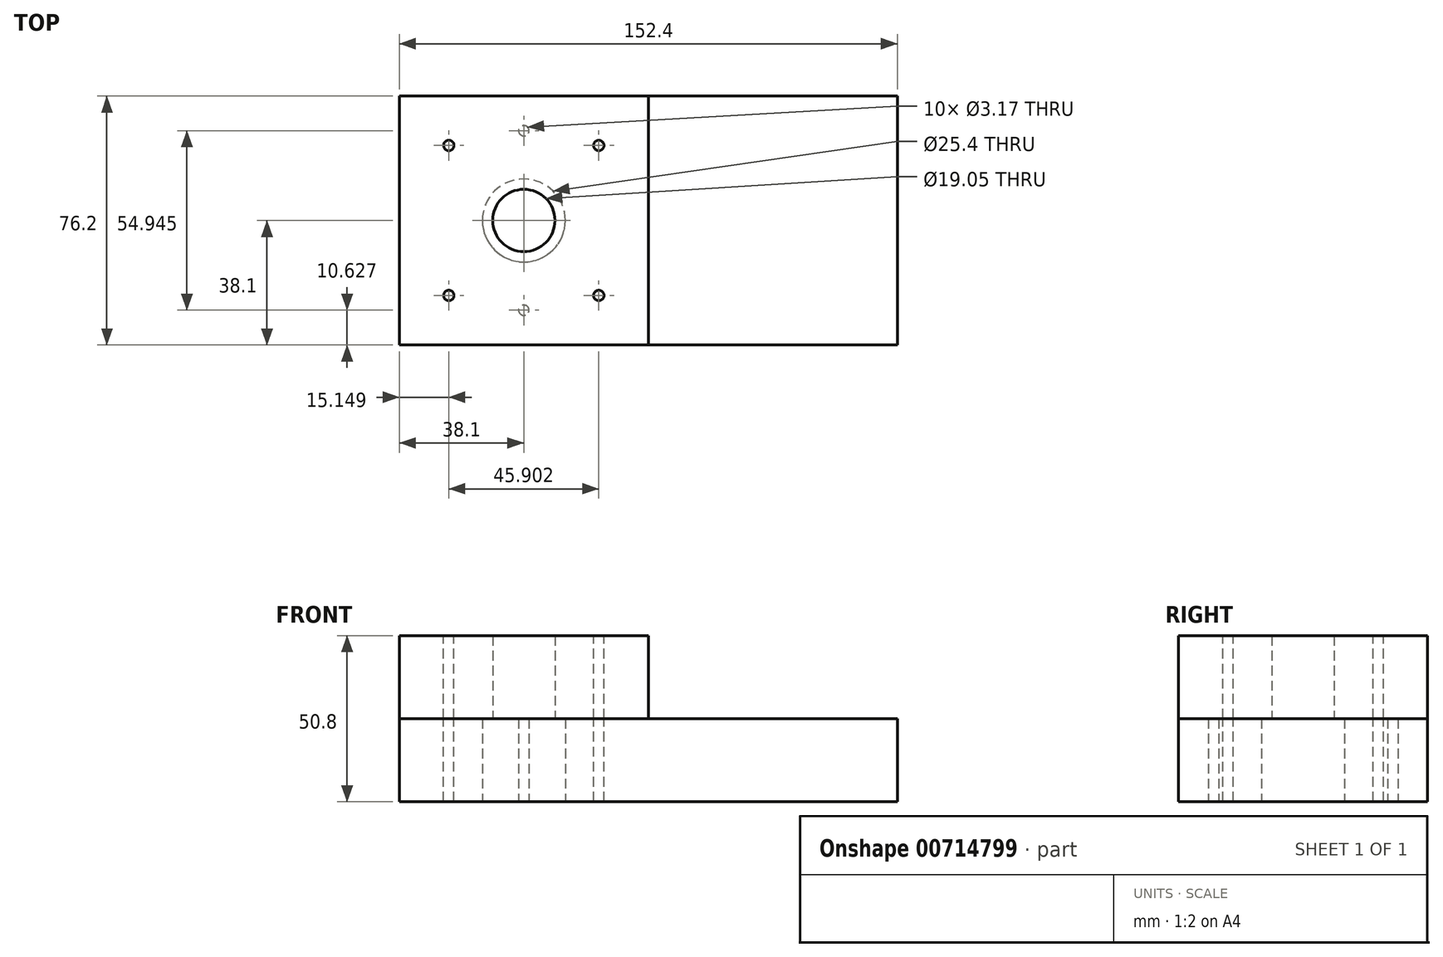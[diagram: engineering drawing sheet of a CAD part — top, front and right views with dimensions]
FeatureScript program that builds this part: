
annotation { "Feature Type Name" : "Feature", "Feature Type Description" : "" }
export const myFeature = defineFeature(function(context is Context, id is Id, definition is map)
    precondition{}
    {
        {
            var Q0;
            Q0=qCreatedBy(makeId("Top.planeOp"),FACE);
            var sketch = newSketch(context, id + "F0", { "sketchPlane" : qUnion([Q0])});
            skLineSegment(sketch, "E0.bottom", {"start": v(76.2, 38.1) * mm, "end": v(-76.2, 38.1) * mm});
            skLineSegment(sketch, "E0.top", {"start": v(76.2, -38.1) * mm, "end": v(-76.2, -38.1) * mm});
            skLineSegment(sketch, "E0.left", {"start": v(76.2, 38.1) * mm, "end": v(76.2, -38.1) * mm});
            skLineSegment(sketch, "E0.right", {"start": v(-76.2, 38.1) * mm, "end": v(-76.2, -38.1) * mm});
            skPoint(sketch, "E0.middle", {"position": v(0, 0) * mm});
            skSolve(sketch);
        }
        {
            var Q0;
            Q0=qCreatedBy(makeId("Top.planeOp"),FACE);
            var sketch = newSketch(context, id + "F1", { "sketchPlane" : qUnion([Q0])});
            skPoint(sketch, "E1", {"position": v(0, 0) * mm});
            skPoint(sketch, "E2", {"position": v(-38.1, 27.47) * mm});
            skPoint(sketch, "E3.1.0", {"position": v(-38.1, -27.47) * mm});
            skPoint(sketch, "E3.center", {"position": v(-38.1, 0) * mm});
            skSolve(sketch);
        }
        {
            var Q0;
            Q0 = qSketchRegion(id + "F0", true);
            extrude(context, id + "F2", {"entities" : qUnion([Q0]), "depth" : 25.4 * mm, "offsetDistance" : 25.4 * mm});
        }
        {
            var Q0;
            Q0=makeQuery(id+"F2.opExtrude","CAP_FACE",FACE,{"disambiguationData":[OSD([sQuery(id+"F0.wireOp",EDGE,"E0.bottom"),sQuery(id+"F0.wireOp",EDGE,"E0.top"),sQuery(id+"F0.wireOp",EDGE,"E0.left"),sQuery(id+"F0.wireOp",EDGE,"E0.right")])],"isStart":false});
            var sketch = newSketch(context, id + "F3", { "sketchPlane" : qUnion([Q0])});
            skLineSegment(sketch, "E4.bottom", {"start": v(-76.2, 38.1) * mm, "end": v(0, 38.1) * mm});
            skLineSegment(sketch, "E4.top", {"start": v(-76.2, -38.1) * mm, "end": v(76.2, -38.1) * mm});
            skLineSegment(sketch, "E4.left", {"start": v(-76.2, 38.1) * mm, "end": v(-76.2, -38.1) * mm});
            skLineSegment(sketch, "E4.right", {"start": v(0, 38.1) * mm, "end": v(0, -38.1) * mm});
            skSolve(sketch);
        }
        {
            var Q0;
            Q0=sQuery(id+"F1.wireOp",VERTEX,"E3.center");
            var Q1;
            Q1=makeQuery(id+"F2.opExtrude","SWEPT_BODY",BODY,{"disambiguationData":[OSD([sQuery(id+"F0.wireOp",EDGE,"E0.bottom"),sQuery(id+"F0.wireOp",EDGE,"E0.top"),sQuery(id+"F0.wireOp",EDGE,"E0.left"),sQuery(id+"F0.wireOp",EDGE,"E0.right")])]});
            hole(context, id + "F4", {"style" : HoleStyle.SIMPLE, "endStyle" : HoleEndStyle.THROUGH, "oppositeDirection" : true, "holeDiameter" : 25.4 * mm, "majorDiameter" : 6.35 * mm, "isTappedThrough" : true, "tappedDepth" : 12.7 * mm, "tapClearance" : 3, "locations" : qUnion([Q0]), "scope" : qUnion([Q1])});
        }
        {
            var Q0;
            Q0=sQuery(id+"F1.wireOp",VERTEX,"E2");
            var Q1;
            Q1=sQuery(id+"F1.wireOp",VERTEX,"E3.1.0");
            var Q2;
            Q2=makeQuery(id+"F2.opExtrude","SWEPT_BODY",BODY,{"disambiguationData":[OSD([sQuery(id+"F0.wireOp",EDGE,"E0.bottom"),sQuery(id+"F0.wireOp",EDGE,"E0.top"),sQuery(id+"F0.wireOp",EDGE,"E0.left"),sQuery(id+"F0.wireOp",EDGE,"E0.right")])]});
            hole(context, id + "F5", {"style" : HoleStyle.SIMPLE, "endStyle" : HoleEndStyle.THROUGH, "oppositeDirection" : true, "holeDiameter" : 3.17 * mm, "majorDiameter" : 6.35 * mm, "isTappedThrough" : true, "tappedDepth" : 12.7 * mm, "tapClearance" : 3, "locations" : qUnion([Q0, Q1]), "scope" : qUnion([Q2])});
        }
        {
            var Q0;
            Q0 = qSketchRegion(id + "F3", true);
            extrude(context, id + "F6", {"entities" : qUnion([Q0]), "depth" : 25.4 * mm, "offsetDistance" : 25.4 * mm});
        }
        {
            var Q0;
            Q0=makeQuery(id+"F6.opExtrude","CAP_FACE",FACE,{"disambiguationData":[OSD([sQuery(id+"F3.wireOp",EDGE,"E4.bottom"),sQuery(id+"F3.wireOp",EDGE,"E4.top"),sQuery(id+"F3.wireOp",EDGE,"E4.left"),sQuery(id+"F3.wireOp",EDGE,"E4.right")])],"isStart":false});
            var sketch = newSketch(context, id + "F7", { "sketchPlane" : qUnion([Q0])});
            skLineSegment(sketch, "E5", {"start": v(0, 38.1) * mm, "end": v(-15.15, 22.95) * mm, "construction": true});
            skPoint(sketch, "E6", {"position": v(-15.15, 22.95) * mm});
            skPoint(sketch, "E7.1.0", {"position": v(-61.05, 22.95) * mm});
            skPoint(sketch, "E7.2.0", {"position": v(-61.05, -22.95) * mm});
            skPoint(sketch, "E7.3.0", {"position": v(-15.15, -22.95) * mm});
            skPoint(sketch, "E7.center", {"position": v(-38.1, 0) * mm});
            skSolve(sketch);
        }
        {
            var Q0;
            Q0=sQuery(id+"F7.wireOp",VERTEX,"E6");
            var Q1;
            Q1=sQuery(id+"F7.wireOp",VERTEX,"E7.3.0");
            var Q2;
            Q2=sQuery(id+"F7.wireOp",VERTEX,"E7.2.0");
            var Q3;
            Q3=sQuery(id+"F7.wireOp",VERTEX,"E7.1.0");
            var Q4;
            Q4=makeQuery(id+"F2.opExtrude","SWEPT_BODY",BODY,{"disambiguationData":[OSD([sQuery(id+"F0.wireOp",EDGE,"E0.bottom"),sQuery(id+"F0.wireOp",EDGE,"E0.top"),sQuery(id+"F0.wireOp",EDGE,"E0.left"),sQuery(id+"F0.wireOp",EDGE,"E0.right")])]});
            var Q5;
            Q5=makeQuery(id+"F6.opExtrude","SWEPT_BODY",BODY,{"disambiguationData":[OSD([sQuery(id+"F3.wireOp",EDGE,"E4.bottom"),sQuery(id+"F3.wireOp",EDGE,"E4.top"),sQuery(id+"F3.wireOp",EDGE,"E4.left"),sQuery(id+"F3.wireOp",EDGE,"E4.right")])]});
            hole(context, id + "F8", {"style" : HoleStyle.SIMPLE, "endStyle" : HoleEndStyle.THROUGH, "holeDiameter" : 3.17 * mm, "majorDiameter" : 6.35 * mm, "isTappedThrough" : true, "tappedDepth" : 12.7 * mm, "tapClearance" : 3, "locations" : qUnion([Q0, Q1, Q2, Q3]), "scope" : qUnion([Q4, Q5])});
        }
        {
            var Q0;
            Q0=sQuery(id+"F1.wireOp",VERTEX,"E3.center");
            var Q1;
            Q1=makeQuery(id+"F6.opExtrude","SWEPT_BODY",BODY,{"disambiguationData":[OSD([sQuery(id+"F3.wireOp",EDGE,"E4.bottom"),sQuery(id+"F3.wireOp",EDGE,"E4.top"),sQuery(id+"F3.wireOp",EDGE,"E4.left"),sQuery(id+"F3.wireOp",EDGE,"E4.right")])]});
            hole(context, id + "F9", {"style" : HoleStyle.SIMPLE, "endStyle" : HoleEndStyle.THROUGH, "oppositeDirection" : true, "holeDiameter" : 19.05 * mm, "majorDiameter" : 6.35 * mm, "isTappedThrough" : true, "tappedDepth" : 12.7 * mm, "tapClearance" : 3, "locations" : qUnion([Q0]), "scope" : qUnion([Q1])});
        }
    });
